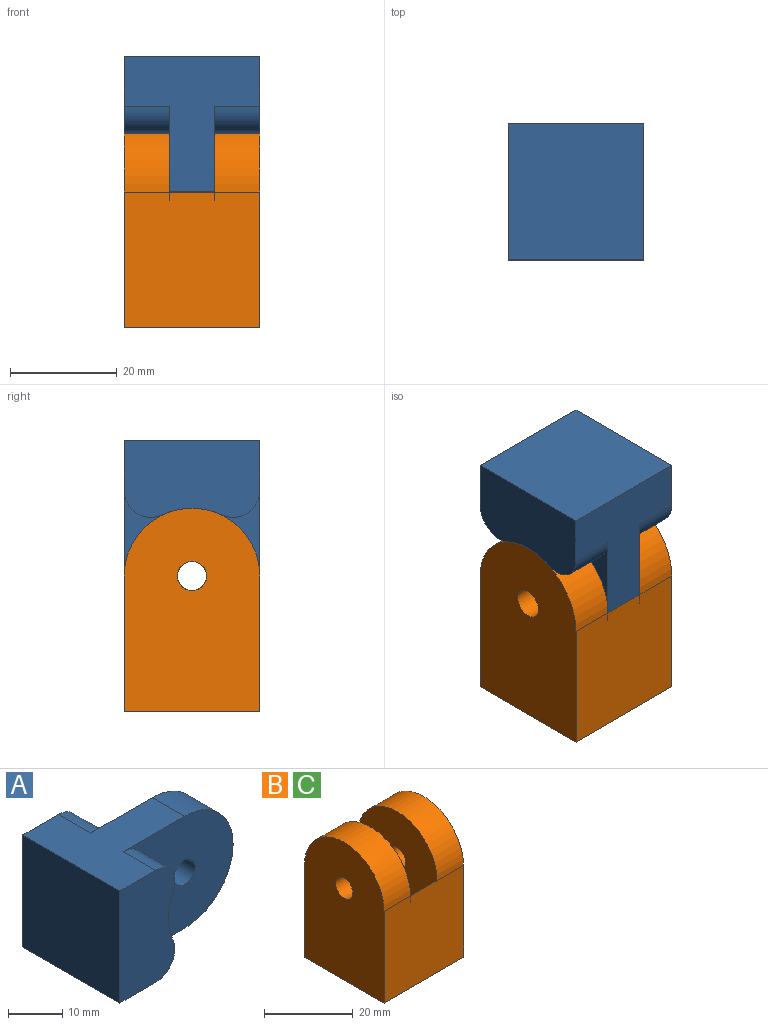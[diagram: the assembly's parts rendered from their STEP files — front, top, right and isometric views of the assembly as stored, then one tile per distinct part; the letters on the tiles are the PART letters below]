
ASSEMBLY  parts=3 mates=1
PART A: 15 faces, bbox 38.1x25.4x25.4 mm
  f0: plane 25.4x25.4mm, normal (0,0,1), area 373.1mm2, adj f1,f3,f4,f5,f6,f7,f12,f14
  f1: plane 25.4x25.4mm, normal (-1,0,0), area 645.2mm2, adj f0,f2,f3,f4
  f2: plane 25.4x25.4mm, normal (0,0,-1), area 373.1mm2, adj f1,f3,f4,f5,f6,f7,f11,f13
  f3: plane 25.4x14.42mm, normal (0,-1,0), area 340.1mm2, adj f0,f1,f2,f8,f13,f14
  f4: plane 25.4x14.42mm, normal (0,1,0), area 340.1mm2, adj f0,f1,f2,f9,f11,f12
  f5: plane 28.76x25.4mm, normal (0,-1,0), area 534.7mm2, adj f0,f2,f6,f8,f10,f13,f14
  f6: cylinder r=12.7mm len=25.4mm, axis (0,-1,0), area 337.8mm2, adj f0,f2,f5,f7
  f7: plane 28.76x25.4mm, normal (0,1,0), area 534.7mm2, adj f0,f2,f6,f9,f10,f11,f12
  f8: cylinder r=12.7mm len=10.89mm, axis (0,1,0), area 95.2mm2, adj f3,f5,f13,f14
  f9: cylinder r=12.7mm len=10.89mm, axis (0,1,0), area 95.2mm2, adj f4,f7,f11,f12
  f10: cylinder r=2.75mm len=8.47mm, axis (0,-1,0), area 146.3mm2, adj f5,f7
  f11: cylinder r=5.08mm len=8.47mm, axis (0,1,0), area 86.6mm2, adj f2,f4,f7,f9
  f12: cylinder r=5.08mm len=8.47mm, axis (0,1,0), area 86.6mm2, adj f0,f4,f7,f9
  f13: cylinder r=5.08mm len=8.47mm, axis (0,1,0), area 86.6mm2, adj f2,f3,f5,f8
  f14: cylinder r=5.08mm len=8.47mm, axis (0,1,0), area 86.6mm2, adj f0,f3,f5,f8
PART B: 13 faces, bbox 25.4x25.4x38.1 mm
  f0: plane 38.1x25.4mm, normal (-1,0,0), area 874.8mm2, adj f1,f3,f4,f8,f11
  f1: plane 25.4x25.4mm, normal (0,0,-1), area 645.2mm2, adj f0,f2,f3,f4
  f2: plane 38.1x25.4mm, normal (1,0,0), area 874.8mm2, adj f1,f3,f4,f6,f10
  f3: plane 25.4x25.4mm, normal (0,1,0), area 509.1mm2, adj f0,f1,f2,f5,f6,f7,f8,f12
  f4: plane 25.4x25.4mm, normal (0,-1,0), area 645.2mm2, adj f0,f1,f2,f6,f8,f9
  f5: plane 28.76x25.4mm, normal (-1,0,0), area 508.8mm2, adj f3,f6,f9,f10,f12
  f6: cylinder r=12.7mm len=25.4mm, axis (-1,0,0), area 337.8mm2, adj f2,f3,f4,f5
  f7: plane 28.76x25.4mm, normal (1,0,0), area 508.8mm2, adj f3,f8,f9,f11,f12
  f8: cylinder r=12.7mm len=25.4mm, axis (-1,0,0), area 337.8mm2, adj f0,f3,f4,f7
  f9: cylinder r=12.7mm len=18.14mm, axis (1,0,0), area 216.5mm2, adj f4,f5,f7,f12
  f10: cylinder r=2.75mm len=8.47mm, axis (1,0,0), area 146.3mm2, adj f2,f5
  f11: cylinder r=2.75mm len=8.47mm, axis (-1,0,0), area 146.3mm2, adj f0,f7
  f12: cylinder r=5.08mm len=8.47mm, axis (1,0,0), area 86.6mm2, adj f3,f5,f7,f9
PART C: same geometry as B
PLACE A rot(axis=(-0.58,0.58,0.58),120deg) t=(-16.07,17.07,40.32)mm
PLACE B t=(-8.91,-8.33,4.03)mm
PLACE C t=(-8.91,-8.33,4.03)mm
MATE revolute A.f6 <-> B.f6  axis (1,0,0) through (0.86,4.37,14.92)mm
